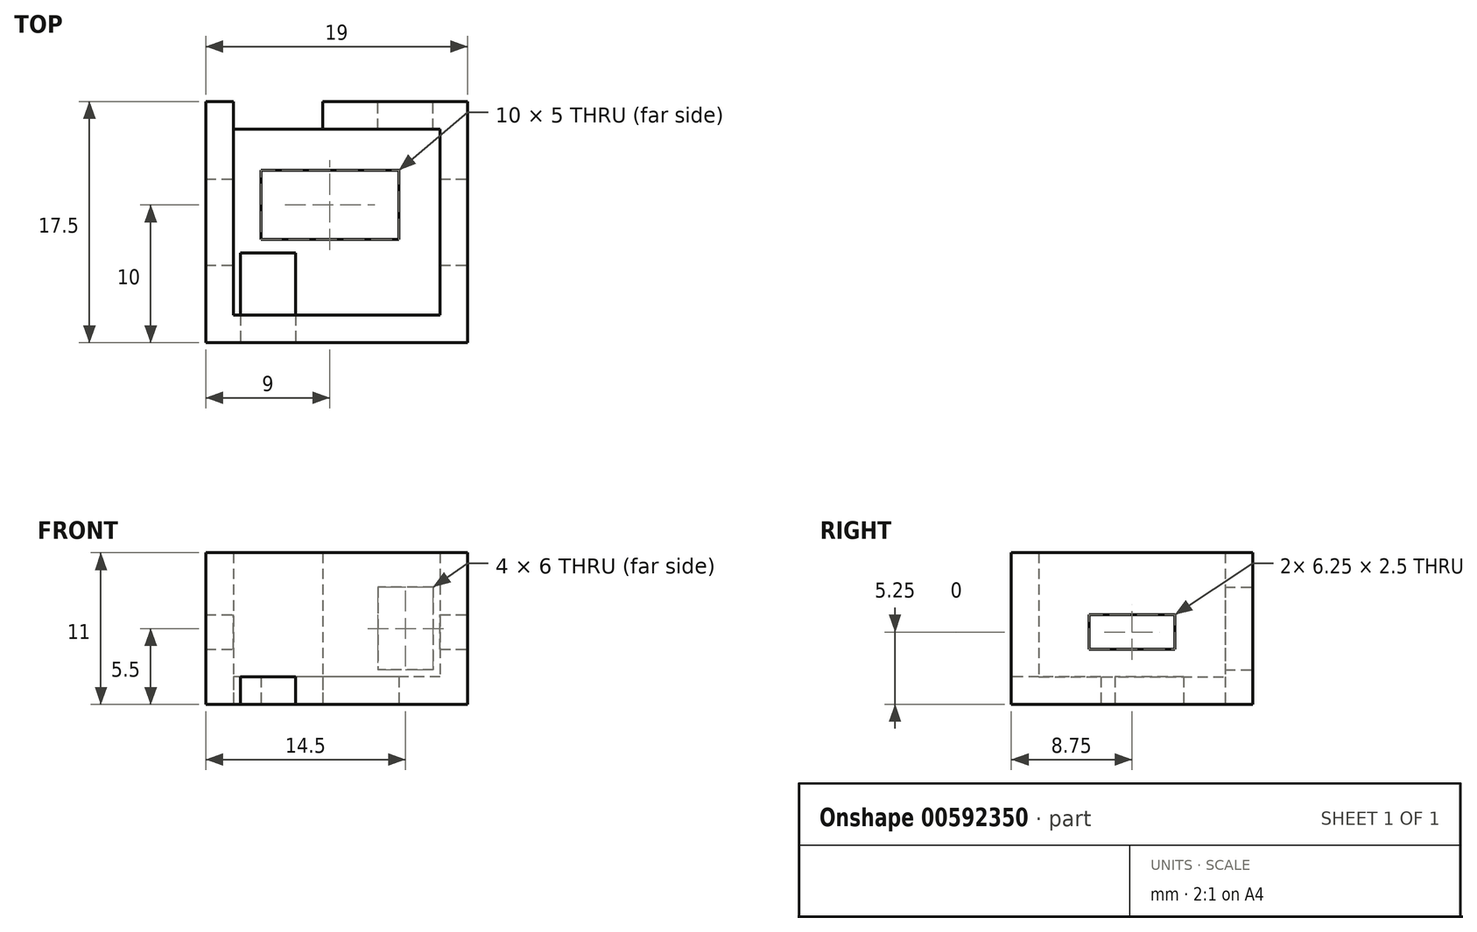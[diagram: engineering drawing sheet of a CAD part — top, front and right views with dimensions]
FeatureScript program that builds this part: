
annotation { "Feature Type Name" : "Feature", "Feature Type Description" : "" }
export const myFeature = defineFeature(function(context is Context, id is Id, definition is map)
    precondition{}
    {
        {
            var Q0;
            Q0=qCreatedBy(makeId("Top.planeOp"),FACE);
            var sketch = newSketch(context, id + "F0", { "sketchPlane" : qUnion([Q0])});
            skLineSegment(sketch, "E0.bottom", {"start": v(7.5, -6.75) * mm, "end": v(-7.5, -6.75) * mm});
            skLineSegment(sketch, "E0.top", {"start": v(7.5, 6.75) * mm, "end": v(-7.5, 6.75) * mm});
            skLineSegment(sketch, "E0.left", {"start": v(7.5, -6.75) * mm, "end": v(7.5, 6.75) * mm});
            skLineSegment(sketch, "E0.right", {"start": v(-7.5, -6.75) * mm, "end": v(-7.5, 6.75) * mm});
            skPoint(sketch, "E0.middle", {"position": v(0, 0) * mm});
            skLineSegment(sketch, "E1.bottom", {"start": v(-9.5, -8.75) * mm, "end": v(9.5, -8.75) * mm});
            skLineSegment(sketch, "E1.top", {"start": v(-9.5, 8.75) * mm, "end": v(9.5, 8.75) * mm});
            skLineSegment(sketch, "E1.left", {"start": v(-9.5, -8.75) * mm, "end": v(-9.5, 8.75) * mm});
            skLineSegment(sketch, "E1.right", {"start": v(9.5, -8.75) * mm, "end": v(9.5, 8.75) * mm});
            skLineSegment(sketch, "E2.bottom", {"start": v(4.5, 3.75) * mm, "end": v(-5.5, 3.75) * mm});
            skLineSegment(sketch, "E2.top", {"start": v(4.5, -1.25) * mm, "end": v(-5.5, -1.25) * mm});
            skLineSegment(sketch, "E2.left", {"start": v(4.5, 3.75) * mm, "end": v(4.5, -1.25) * mm});
            skLineSegment(sketch, "E2.right", {"start": v(-5.5, 3.75) * mm, "end": v(-5.5, -1.25) * mm});
            skLineSegment(sketch, "E3.bottom", {"start": v(-3, -2.25) * mm, "end": v(-7, -2.25) * mm});
            skLineSegment(sketch, "E3.top", {"start": v(-3, -6.25) * mm, "end": v(-7, -6.25) * mm});
            skLineSegment(sketch, "E3.left", {"start": v(-3, -2.25) * mm, "end": v(-3, -6.25) * mm});
            skLineSegment(sketch, "E3.right", {"start": v(-7, -2.25) * mm, "end": v(-7, -6.25) * mm});
            skLineSegment(sketch, "E4", {"start": v(-7.5, 6.75) * mm, "end": v(-7.5, 8.75) * mm});
            skLineSegment(sketch, "E5", {"start": v(-1, 8.75) * mm, "end": v(-1, 6.75) * mm});
            skSolve(sketch);
        }
        {
            var Q0;
            Q0=makeQuery(id+"F0.imprint","IMPRINT",FACE,{"disambiguationData":[TD([[makeQuery(id+"F0.imprint","IMPRINT",EDGE,{"derivedFrom":sQuery(id+"F0.wireOp",EDGE,"E0.bottom")}),-1.0]])]});
            extrude(context, id + "F1", {"entities" : qUnion([Q0]), "depth" : 2 * mm, "offsetDistance" : 25 * mm});
        }
        {
            var Q0;
            Q0=makeQuery(id+"F0.imprint","IMPRINT",FACE,{"disambiguationData":[TD([[makeQuery(id+"F0.imprint","IMPRINT",EDGE,{"derivedFrom":sQuery(id+"F0.wireOp",EDGE,"E0.bottom")}),1.0]])]});
            extrude(context, id + "F2", {"entities" : qUnion([Q0]), "operationType" : NewBodyOperationType.ADD, "depth" : 11 * mm, "offsetDistance" : 25 * mm});
        }
        {
            var Q0;
            {var subQ0=sQuery(id+"F0.wireOp",EDGE,"E1.top");Q0=makeQuery(id+"F2.opExtrude","SWEPT_FACE",FACE,{"disambiguationData":[OSD([subQ0]),TDD([makeQuery(id+"F0.imprint","IMPRINT",EDGE,{"disambiguationData":[TD([[makeQuery(id+"F0.imprint","INTERSECT",VERTEX,{"derivedFrom":[subQ0,sQuery(id+"F0.wireOp",EDGE,"E1.right")]}),1.0]])],"derivedFrom":subQ0})])]});}
            var sketch = newSketch(context, id + "F3", { "sketchPlane" : qUnion([Q0])});
            skLineSegment(sketch, "E6.bottom", {"start": v(-3, 2.5) * mm, "end": v(-7, 2.5) * mm});
            skLineSegment(sketch, "E6.top", {"start": v(-3, 8.5) * mm, "end": v(-7, 8.5) * mm});
            skLineSegment(sketch, "E6.left", {"start": v(-3, 2.5) * mm, "end": v(-3, 8.5) * mm});
            skLineSegment(sketch, "E6.right", {"start": v(-7, 2.5) * mm, "end": v(-7, 8.5) * mm});
            skSolve(sketch);
        }
        {
            var Q0;
            Q0=makeQuery(id+"F3.imprint","IMPRINT",FACE,{"disambiguationData":[TD([[makeQuery(id+"F3.imprint","IMPRINT",EDGE,{"derivedFrom":sQuery(id+"F3.wireOp",EDGE,"E6.bottom")}),-1.0]])]});
            extrude(context, id + "F4", {"entities" : qUnion([Q0]), "operationType" : NewBodyOperationType.REMOVE, "oppositeDirection" : true, "depth" : 2.9 * mm, "offsetDistance" : 25 * mm});
        }
        {
            var Q0;
            Q0=makeQuery(id+"F2.opExtrude","SWEPT_FACE",FACE,{"disambiguationData":[OSD([sQuery(id+"F0.wireOp",EDGE,"E1.right")])]});
            var sketch = newSketch(context, id + "F5", { "sketchPlane" : qUnion([Q0])});
            skLineSegment(sketch, "E7.bottom", {"start": v(-3.13, 6.5) * mm, "end": v(3.12, 6.5) * mm});
            skLineSegment(sketch, "E7.top", {"start": v(-3.13, 4) * mm, "end": v(3.12, 4) * mm});
            skLineSegment(sketch, "E7.left", {"start": v(-3.13, 6.5) * mm, "end": v(-3.13, 4) * mm});
            skLineSegment(sketch, "E7.right", {"start": v(3.12, 6.5) * mm, "end": v(3.12, 4) * mm});
            skSolve(sketch);
        }
        {
            var Q0;
            Q0=makeQuery(id+"F5.imprint","IMPRINT",FACE,{"disambiguationData":[TD([[makeQuery(id+"F5.imprint","IMPRINT",EDGE,{"derivedFrom":sQuery(id+"F5.wireOp",EDGE,"E7.bottom")}),-1.0]])]});
            extrude(context, id + "F6", {"entities" : qUnion([Q0]), "operationType" : NewBodyOperationType.REMOVE, "oppositeDirection" : true, "depth" : 20 * mm, "offsetDistance" : 25 * mm});
        }
        {
            var Q0;
            Q0=makeQuery(id+"F2.opExtrude","SWEPT_FACE",FACE,{"disambiguationData":[OSD([sQuery(id+"F0.wireOp",EDGE,"E1.bottom")])]});
            var sketch = newSketch(context, id + "F7", { "sketchPlane" : qUnion([Q0])});
            skLineSegment(sketch, "E8.bottom", {"start": v(-7, 0) * mm, "end": v(-3, 0) * mm});
            skLineSegment(sketch, "E8.top", {"start": v(-7, 2) * mm, "end": v(-3, 2) * mm});
            skLineSegment(sketch, "E8.left", {"start": v(-7, 0) * mm, "end": v(-7, 2) * mm});
            skLineSegment(sketch, "E8.right", {"start": v(-3, 0) * mm, "end": v(-3, 2) * mm});
            skSolve(sketch);
        }
        {
            var Q0;
            Q0=makeQuery(id+"F7.imprint","IMPRINT",FACE,{"disambiguationData":[TD([[makeQuery(id+"F7.imprint","IMPRINT",EDGE,{"derivedFrom":sQuery(id+"F7.wireOp",EDGE,"E8.bottom")}),1.0]])]});
            extrude(context, id + "F8", {"entities" : qUnion([Q0]), "operationType" : NewBodyOperationType.REMOVE, "oppositeDirection" : true, "depth" : 2.8 * mm, "offsetDistance" : 25 * mm});
        }
    });
